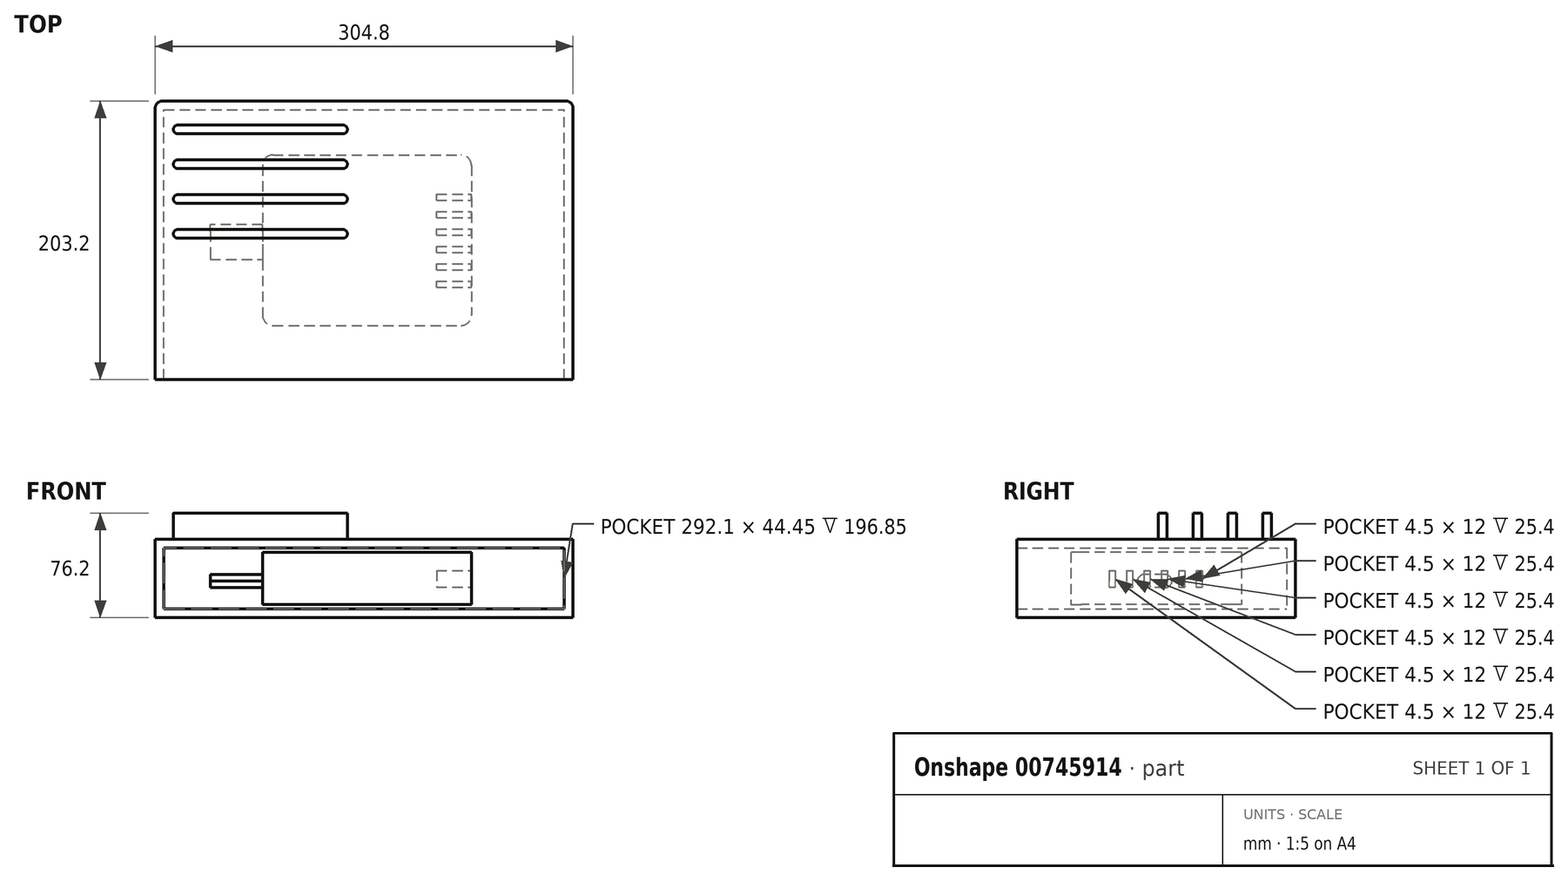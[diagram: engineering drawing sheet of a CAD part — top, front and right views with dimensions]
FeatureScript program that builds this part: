
annotation { "Feature Type Name" : "Feature", "Feature Type Description" : "" }
export const myFeature = defineFeature(function(context is Context, id is Id, definition is map)
    precondition{}
    {
        {
            var Q0;
            Q0=qCreatedBy(makeId("Top.planeOp"),FACE);
            var sketch = newSketch(context, id + "F0", { "sketchPlane" : qUnion([Q0])});
            skLineSegment(sketch, "E0.bottom", {"start": v(-76.2, 62.23) * mm, "end": v(76.2, 62.23) * mm});
            skLineSegment(sketch, "E0.top", {"start": v(-76.2, -62.23) * mm, "end": v(76.2, -62.23) * mm});
            skLineSegment(sketch, "E0.left", {"start": v(-76.2, 62.23) * mm, "end": v(-76.2, -62.23) * mm});
            skLineSegment(sketch, "E0.right", {"start": v(76.2, 62.23) * mm, "end": v(76.2, -62.23) * mm});
            skSolve(sketch);
        }
        {
            var Q0;
            Q0 = qSketchRegion(id + "F0", true);
            extrude(context, id + "F1", {"entities" : qUnion([Q0]), "depth" : 38.1 * mm, "offsetDistance" : 25.4 * mm});
        }
        {
            var Q0;
            Q0=makeQuery(id+"F1.opExtrude","SWEPT_EDGE",EDGE,{"disambiguationData":[OSD([sQuery(id+"F0.wireOp",EDGE,"E0.top"),sQuery(id+"F0.wireOp",EDGE,"E0.left")])]});
            var Q1;
            Q1=makeQuery(id+"F1.opExtrude","SWEPT_EDGE",EDGE,{"disambiguationData":[OSD([sQuery(id+"F0.wireOp",EDGE,"E0.top"),sQuery(id+"F0.wireOp",EDGE,"E0.right")])]});
            var Q2;
            Q2=makeQuery(id+"F1.opExtrude","SWEPT_EDGE",EDGE,{"disambiguationData":[OSD([sQuery(id+"F0.wireOp",EDGE,"E0.bottom"),sQuery(id+"F0.wireOp",EDGE,"E0.right")])]});
            var Q3;
            Q3=makeQuery(id+"F1.opExtrude","SWEPT_EDGE",EDGE,{"disambiguationData":[OSD([sQuery(id+"F0.wireOp",EDGE,"E0.bottom"),sQuery(id+"F0.wireOp",EDGE,"E0.left")])]});
            fillet(context, id + "F2", {"entities" : qUnion([Q0, Q1, Q2, Q3]), "radius" : 7.62 * mm, "tangentPropagation" : true, "allowEdgeOverflow" : false});
        }
        {
            var Q0;
            Q0=makeQuery(id+"F1.opExtrude","SWEPT_FACE",FACE,{"disambiguationData":[OSD([sQuery(id+"F0.wireOp",EDGE,"E0.right")])]});
            var sketch = newSketch(context, id + "F3", { "sketchPlane" : qUnion([Q0])});
            skLineSegment(sketch, "E1.bottom", {"start": v(-34.3, 24.73) * mm, "end": v(-29.79, 24.73) * mm});
            skLineSegment(sketch, "E1.top", {"start": v(-34.3, 12.73) * mm, "end": v(-29.79, 12.73) * mm});
            skLineSegment(sketch, "E1.left", {"start": v(-34.3, 24.73) * mm, "end": v(-34.3, 12.73) * mm});
            skLineSegment(sketch, "E1.right", {"start": v(-29.79, 24.73) * mm, "end": v(-29.79, 12.73) * mm});
            skLineSegment(sketch, "E2.1.0.0", {"start": v(-17.09, 24.73) * mm, "end": v(-17.09, 12.73) * mm});
            skLineSegment(sketch, "E2.1.0.1", {"start": v(-21.59, 12.73) * mm, "end": v(-17.09, 12.73) * mm});
            skLineSegment(sketch, "E2.1.0.2", {"start": v(-21.59, 24.73) * mm, "end": v(-21.59, 12.73) * mm});
            skLineSegment(sketch, "E2.1.0.3", {"start": v(-21.59, 24.73) * mm, "end": v(-17.09, 24.73) * mm});
            skLineSegment(sketch, "E2.2.0.0", {"start": v(-4.39, 24.73) * mm, "end": v(-4.39, 12.73) * mm});
            skLineSegment(sketch, "E2.2.0.1", {"start": v(-8.89, 12.73) * mm, "end": v(-4.39, 12.73) * mm});
            skLineSegment(sketch, "E2.2.0.2", {"start": v(-8.89, 24.73) * mm, "end": v(-8.89, 12.73) * mm});
            skLineSegment(sketch, "E2.2.0.3", {"start": v(-8.89, 24.73) * mm, "end": v(-4.39, 24.73) * mm});
            skLineSegment(sketch, "E2.3.0.0", {"start": v(8.31, 24.73) * mm, "end": v(8.31, 12.73) * mm});
            skLineSegment(sketch, "E2.3.0.1", {"start": v(3.81, 12.73) * mm, "end": v(8.31, 12.73) * mm});
            skLineSegment(sketch, "E2.3.0.2", {"start": v(3.81, 24.73) * mm, "end": v(3.81, 12.73) * mm});
            skLineSegment(sketch, "E2.3.0.3", {"start": v(3.81, 24.73) * mm, "end": v(8.31, 24.73) * mm});
            skLineSegment(sketch, "E2.4.0.0", {"start": v(21.01, 24.73) * mm, "end": v(21.01, 12.73) * mm});
            skLineSegment(sketch, "E2.4.0.1", {"start": v(16.51, 12.73) * mm, "end": v(21.01, 12.73) * mm});
            skLineSegment(sketch, "E2.4.0.2", {"start": v(16.51, 24.73) * mm, "end": v(16.51, 12.73) * mm});
            skLineSegment(sketch, "E2.4.0.3", {"start": v(16.51, 24.73) * mm, "end": v(21.01, 24.73) * mm});
            skLineSegment(sketch, "E2.5.0.0", {"start": v(33.71, 24.73) * mm, "end": v(33.71, 12.73) * mm});
            skLineSegment(sketch, "E2.5.0.1", {"start": v(29.21, 12.73) * mm, "end": v(33.71, 12.73) * mm});
            skLineSegment(sketch, "E2.5.0.2", {"start": v(29.21, 24.73) * mm, "end": v(29.21, 12.73) * mm});
            skLineSegment(sketch, "E2.5.0.3", {"start": v(29.21, 24.73) * mm, "end": v(33.71, 24.73) * mm});
            skLineSegment(sketch, "E2.direction1", {"start": v(-29.79, 12.73) * mm, "end": v(-17.09, 12.73) * mm, "construction": true});
            skSolve(sketch);
        }
        {
            var Q0;
            Q0=makeQuery(id+"F3.imprint","IMPRINT",FACE,{"disambiguationData":[TD([[makeQuery(id+"F3.imprint","IMPRINT",EDGE,{"derivedFrom":sQuery(id+"F3.wireOp",EDGE,"E1.bottom")}),-1.0]])]});
            var Q1;
            Q1=makeQuery(id+"F3.imprint","IMPRINT",FACE,{"disambiguationData":[TD([[makeQuery(id+"F3.imprint","IMPRINT",EDGE,{"derivedFrom":sQuery(id+"F3.wireOp",EDGE,"E2.1.0.0")}),-1.0]])]});
            var Q2;
            Q2=makeQuery(id+"F3.imprint","IMPRINT",FACE,{"disambiguationData":[TD([[makeQuery(id+"F3.imprint","IMPRINT",EDGE,{"derivedFrom":sQuery(id+"F3.wireOp",EDGE,"E2.2.0.0")}),-1.0]])]});
            var Q3;
            Q3=makeQuery(id+"F3.imprint","IMPRINT",FACE,{"disambiguationData":[TD([[makeQuery(id+"F3.imprint","IMPRINT",EDGE,{"derivedFrom":sQuery(id+"F3.wireOp",EDGE,"E2.3.0.0")}),-1.0]])]});
            var Q4;
            Q4=makeQuery(id+"F3.imprint","IMPRINT",FACE,{"disambiguationData":[TD([[makeQuery(id+"F3.imprint","IMPRINT",EDGE,{"derivedFrom":sQuery(id+"F3.wireOp",EDGE,"E2.4.0.0")}),-1.0]])]});
            var Q5;
            Q5=makeQuery(id+"F3.imprint","IMPRINT",FACE,{"disambiguationData":[TD([[makeQuery(id+"F3.imprint","IMPRINT",EDGE,{"derivedFrom":sQuery(id+"F3.wireOp",EDGE,"E2.5.0.0")}),-1.0]])]});
            extrude(context, id + "F4", {"entities" : qUnion([Q0, Q1, Q2, Q3, Q4, Q5]), "operationType" : NewBodyOperationType.REMOVE, "oppositeDirection" : true, "depth" : 25.4 * mm, "offsetDistance" : 25.4 * mm});
        }
        {
            var Q0;
            Q0=makeQuery(id+"F1.opExtrude","SWEPT_FACE",FACE,{"disambiguationData":[OSD([sQuery(id+"F0.wireOp",EDGE,"E0.left")])]});
            var sketch = newSketch(context, id + "F5", { "sketchPlane" : qUnion([Q0])});
            skLineSegment(sketch, "E3.bottom", {"start": v(-11.55, 21.87) * mm, "end": v(13.85, 21.87) * mm});
            skLineSegment(sketch, "E3.top", {"start": v(-11.55, 12.34) * mm, "end": v(13.85, 12.34) * mm});
            skLineSegment(sketch, "E3.left", {"start": v(-11.55, 21.87) * mm, "end": v(-11.55, 12.34) * mm});
            skLineSegment(sketch, "E3.right", {"start": v(13.85, 21.87) * mm, "end": v(13.85, 12.34) * mm});
            skSolve(sketch);
        }
        {
            var Q0;
            Q0=makeQuery(id+"F5.imprint","IMPRINT",FACE,{"disambiguationData":[TD([[makeQuery(id+"F5.imprint","IMPRINT",EDGE,{"derivedFrom":sQuery(id+"F5.wireOp",EDGE,"E3.bottom")}),-1.0]])]});
            extrude(context, id + "F6", {"entities" : qUnion([Q0]), "operationType" : NewBodyOperationType.ADD, "depth" : 38.1 * mm, "offsetDistance" : 25.4 * mm});
        }
        {
            var Q0;
            Q0=makeQuery(id+"F6.opExtrude","SWEPT_EDGE",EDGE,{"disambiguationData":[OSD([sQuery(id+"F5.wireOp",EDGE,"E3.bottom"),sQuery(id+"F5.wireOp",EDGE,"E3.right")])]});
            var Q1;
            Q1=makeQuery(id+"F6.opExtrude","SWEPT_EDGE",EDGE,{"disambiguationData":[OSD([sQuery(id+"F5.wireOp",EDGE,"E3.top"),sQuery(id+"F5.wireOp",EDGE,"E3.right")])]});
            var Q2;
            Q2=makeQuery(id+"F6.opExtrude","SWEPT_EDGE",EDGE,{"disambiguationData":[OSD([sQuery(id+"F5.wireOp",EDGE,"E3.bottom"),sQuery(id+"F5.wireOp",EDGE,"E3.left")])]});
            var Q3;
            Q3=makeQuery(id+"F6.opExtrude","SWEPT_EDGE",EDGE,{"disambiguationData":[OSD([sQuery(id+"F5.wireOp",EDGE,"E3.top"),sQuery(id+"F5.wireOp",EDGE,"E3.left")])]});
            fillet(context, id + "F7", {"entities" : qUnion([Q0, Q1, Q2, Q3]), "radius" : 5.08 * mm, "tangentPropagation" : true, "allowEdgeOverflow" : false});
        }
        {
            var Q0;
            Q0=qCreatedBy(makeId("Front.planeOp"),FACE);
            var sketch = newSketch(context, id + "F8", { "sketchPlane" : qUnion([Q0])});
            skLineSegment(sketch, "E4.bottom", {"start": v(-154.41, 47.62) * mm, "end": v(150.39, 47.62) * mm});
            skLineSegment(sketch, "E4.top", {"start": v(-154.41, -9.52) * mm, "end": v(150.39, -9.52) * mm});
            skLineSegment(sketch, "E4.left", {"start": v(-154.41, 47.62) * mm, "end": v(-154.41, -9.52) * mm});
            skLineSegment(sketch, "E4.right", {"start": v(150.39, 47.62) * mm, "end": v(150.39, -9.52) * mm});
            skSolve(sketch);
        }
        {
            var Q0;
            Q0=makeQuery(id+"F8.imprint","IMPRINT",FACE,{"disambiguationData":[TD([[makeQuery(id+"F8.imprint","IMPRINT",EDGE,{"derivedFrom":sQuery(id+"F8.wireOp",EDGE,"E4.bottom")}),-1.0]])]});
            extrude(context, id + "F9", {"entities" : qUnion([Q0]), "endBound" : BoundingType.SYMMETRIC, "depth" : 203.2 * mm, "offsetDistance" : 25.4 * mm});
        }
        {
            var Q0;
            Q0=makeQuery(id+"F9.opExtrude","CAP_FACE",FACE,{"disambiguationData":[OSD([sQuery(id+"F8.wireOp",EDGE,"E4.bottom"),sQuery(id+"F8.wireOp",EDGE,"E4.top"),sQuery(id+"F8.wireOp",EDGE,"E4.left"),sQuery(id+"F8.wireOp",EDGE,"E4.right")])],"isStart":false});
            shell(context, id + "F10", {"entities" : qUnion([Q0]), "thickness" : 6.35 * mm});
        }
        {
            var Q0;
            Q0=makeQuery(id+"F9.opExtrude","CAP_EDGE",EDGE,{"disambiguationData":[OSD([sQuery(id+"F8.wireOp",EDGE,"E4.left")])],"isStart":true});
            var Q1;
            Q1=makeQuery(id+"F9.opExtrude","CAP_EDGE",EDGE,{"disambiguationData":[OSD([sQuery(id+"F8.wireOp",EDGE,"E4.right")])],"isStart":true});
            fillet(context, id + "F11", {"entities" : qUnion([Q0, Q1]), "radius" : 5.08 * mm, "tangentPropagation" : true, "allowEdgeOverflow" : false});
        }
        {
            var Q0;
            Q0=makeQuery(id+"F9.opExtrude","SWEPT_FACE",FACE,{"disambiguationData":[OSD([sQuery(id+"F8.wireOp",EDGE,"E4.bottom")])]});
            var sketch = newSketch(context, id + "F12", { "sketchPlane" : qUnion([Q0])});
            skLineSegment(sketch, "E5.bottom", {"start": v(-14.23, 77.69) * mm, "end": v(-141.23, 77.69) * mm});
            skLineSegment(sketch, "E5.top", {"start": v(-14.23, 84.04) * mm, "end": v(-141.23, 84.04) * mm});
            skLineSegment(sketch, "E5.left", {"start": v(-14.23, 77.69) * mm, "end": v(-14.23, 84.04) * mm});
            skLineSegment(sketch, "E5.right", {"start": v(-141.23, 77.69) * mm, "end": v(-141.23, 84.04) * mm});
            skLineSegment(sketch, "E6.0.1.0", {"start": v(-14.23, 52.29) * mm, "end": v(-141.23, 52.29) * mm});
            skLineSegment(sketch, "E6.0.1.1", {"start": v(-14.23, 52.29) * mm, "end": v(-14.23, 58.64) * mm});
            skLineSegment(sketch, "E6.0.1.2", {"start": v(-14.23, 58.64) * mm, "end": v(-141.23, 58.64) * mm});
            skLineSegment(sketch, "E6.0.1.3", {"start": v(-141.23, 52.29) * mm, "end": v(-141.23, 58.64) * mm});
            skLineSegment(sketch, "E6.0.2.0", {"start": v(-14.23, 26.89) * mm, "end": v(-141.23, 26.89) * mm});
            skLineSegment(sketch, "E6.0.2.1", {"start": v(-14.23, 26.89) * mm, "end": v(-14.23, 33.24) * mm});
            skLineSegment(sketch, "E6.0.2.2", {"start": v(-14.23, 33.24) * mm, "end": v(-141.23, 33.24) * mm});
            skLineSegment(sketch, "E6.0.2.3", {"start": v(-141.23, 26.89) * mm, "end": v(-141.23, 33.24) * mm});
            skLineSegment(sketch, "E6.0.3.0", {"start": v(-14.23, 1.49) * mm, "end": v(-141.23, 1.49) * mm});
            skLineSegment(sketch, "E6.0.3.1", {"start": v(-14.23, 1.49) * mm, "end": v(-14.23, 7.84) * mm});
            skLineSegment(sketch, "E6.0.3.2", {"start": v(-14.23, 7.84) * mm, "end": v(-141.23, 7.84) * mm});
            skLineSegment(sketch, "E6.0.3.3", {"start": v(-141.23, 1.49) * mm, "end": v(-141.23, 7.84) * mm});
            skLineSegment(sketch, "E6.direction1", {"start": v(-141.23, 77.69) * mm, "end": v(-115.83, 77.69) * mm, "construction": true});
            skLineSegment(sketch, "E6.direction2", {"start": v(-141.23, 77.69) * mm, "end": v(-141.23, 52.29) * mm, "construction": true});
            skSolve(sketch);
        }
        {
            var Q0;
            Q0=makeQuery(id+"F12.imprint","IMPRINT",FACE,{"disambiguationData":[TD([[makeQuery(id+"F12.imprint","IMPRINT",EDGE,{"derivedFrom":sQuery(id+"F12.wireOp",EDGE,"E5.bottom")}),-1.0]])]});
            var Q1;
            Q1=makeQuery(id+"F12.imprint","IMPRINT",FACE,{"disambiguationData":[TD([[makeQuery(id+"F12.imprint","IMPRINT",EDGE,{"derivedFrom":sQuery(id+"F12.wireOp",EDGE,"E6.0.1.0")}),-1.0]])]});
            var Q2;
            Q2=makeQuery(id+"F12.imprint","IMPRINT",FACE,{"disambiguationData":[TD([[makeQuery(id+"F12.imprint","IMPRINT",EDGE,{"derivedFrom":sQuery(id+"F12.wireOp",EDGE,"E6.0.2.0")}),-1.0]])]});
            var Q3;
            Q3=makeQuery(id+"F12.imprint","IMPRINT",FACE,{"disambiguationData":[TD([[makeQuery(id+"F12.imprint","IMPRINT",EDGE,{"derivedFrom":sQuery(id+"F12.wireOp",EDGE,"E6.0.3.0")}),-1.0]])]});
            extrude(context, id + "F13", {"entities" : qUnion([Q0, Q1, Q2, Q3]), "operationType" : NewBodyOperationType.ADD, "depth" : 19.05 * mm, "offsetDistance" : 25.4 * mm});
        }
        {
            var Q0;
            Q0=makeQuery(id+"F13.opExtrude","SWEPT_EDGE",EDGE,{"disambiguationData":[OSD([sQuery(id+"F12.wireOp",EDGE,"E5.top"),sQuery(id+"F12.wireOp",EDGE,"E5.right")])]});
            var Q1;
            Q1=makeQuery(id+"F13.opExtrude","SWEPT_EDGE",EDGE,{"disambiguationData":[OSD([sQuery(id+"F12.wireOp",EDGE,"E5.bottom"),sQuery(id+"F12.wireOp",EDGE,"E5.right")])]});
            var Q2;
            Q2=makeQuery(id+"F13.opExtrude","SWEPT_EDGE",EDGE,{"disambiguationData":[OSD([sQuery(id+"F12.wireOp",EDGE,"E6.0.1.2"),sQuery(id+"F12.wireOp",EDGE,"E6.0.1.3")])]});
            var Q3;
            Q3=makeQuery(id+"F13.opExtrude","SWEPT_EDGE",EDGE,{"disambiguationData":[OSD([sQuery(id+"F12.wireOp",EDGE,"E6.0.2.2"),sQuery(id+"F12.wireOp",EDGE,"E6.0.2.3")])]});
            var Q4;
            Q4=makeQuery(id+"F13.opExtrude","SWEPT_EDGE",EDGE,{"disambiguationData":[OSD([sQuery(id+"F12.wireOp",EDGE,"E6.0.3.2"),sQuery(id+"F12.wireOp",EDGE,"E6.0.3.3")])]});
            var Q5;
            Q5=makeQuery(id+"F13.opExtrude","SWEPT_EDGE",EDGE,{"disambiguationData":[OSD([sQuery(id+"F12.wireOp",EDGE,"E6.0.3.0"),sQuery(id+"F12.wireOp",EDGE,"E6.0.3.3")])]});
            var Q6;
            Q6=makeQuery(id+"F13.opExtrude","SWEPT_EDGE",EDGE,{"disambiguationData":[OSD([sQuery(id+"F12.wireOp",EDGE,"E5.bottom"),sQuery(id+"F12.wireOp",EDGE,"E5.left")])]});
            var Q7;
            Q7=makeQuery(id+"F13.opExtrude","SWEPT_EDGE",EDGE,{"disambiguationData":[OSD([sQuery(id+"F12.wireOp",EDGE,"E5.top"),sQuery(id+"F12.wireOp",EDGE,"E5.left")])]});
            var Q8;
            Q8=makeQuery(id+"F13.opExtrude","SWEPT_EDGE",EDGE,{"disambiguationData":[OSD([sQuery(id+"F12.wireOp",EDGE,"E6.0.1.1"),sQuery(id+"F12.wireOp",EDGE,"E6.0.1.2")])]});
            var Q9;
            Q9=makeQuery(id+"F13.opExtrude","SWEPT_EDGE",EDGE,{"disambiguationData":[OSD([sQuery(id+"F12.wireOp",EDGE,"E6.0.1.0"),sQuery(id+"F12.wireOp",EDGE,"E6.0.1.1")])]});
            var Q10;
            Q10=makeQuery(id+"F13.opExtrude","SWEPT_EDGE",EDGE,{"disambiguationData":[OSD([sQuery(id+"F12.wireOp",EDGE,"E6.0.2.1"),sQuery(id+"F12.wireOp",EDGE,"E6.0.2.2")])]});
            var Q11;
            Q11=makeQuery(id+"F13.opExtrude","SWEPT_EDGE",EDGE,{"disambiguationData":[OSD([sQuery(id+"F12.wireOp",EDGE,"E6.0.2.0"),sQuery(id+"F12.wireOp",EDGE,"E6.0.2.1")])]});
            var Q12;
            Q12=makeQuery(id+"F13.opExtrude","SWEPT_EDGE",EDGE,{"disambiguationData":[OSD([sQuery(id+"F12.wireOp",EDGE,"E6.0.3.1"),sQuery(id+"F12.wireOp",EDGE,"E6.0.3.2")])]});
            var Q13;
            Q13=makeQuery(id+"F13.opExtrude","SWEPT_EDGE",EDGE,{"disambiguationData":[OSD([sQuery(id+"F12.wireOp",EDGE,"E6.0.3.0"),sQuery(id+"F12.wireOp",EDGE,"E6.0.3.1")])]});
            var Q14;
            Q14=makeQuery(id+"F13.opExtrude","SWEPT_EDGE",EDGE,{"disambiguationData":[OSD([sQuery(id+"F12.wireOp",EDGE,"E6.0.1.0"),sQuery(id+"F12.wireOp",EDGE,"E6.0.1.3")])]});
            var Q15;
            Q15=makeQuery(id+"F13.opExtrude","SWEPT_EDGE",EDGE,{"disambiguationData":[OSD([sQuery(id+"F12.wireOp",EDGE,"E6.0.2.0"),sQuery(id+"F12.wireOp",EDGE,"E6.0.2.3")])]});
            fillet(context, id + "F14", {"entities" : qUnion([Q0, Q1, Q2, Q3, Q4, Q5, Q6, Q7, Q8, Q9, Q10, Q11, Q12, Q13, Q14, Q15]), "radius" : 3.17 * mm, "tangentPropagation" : true, "allowEdgeOverflow" : false});
        }
    });
